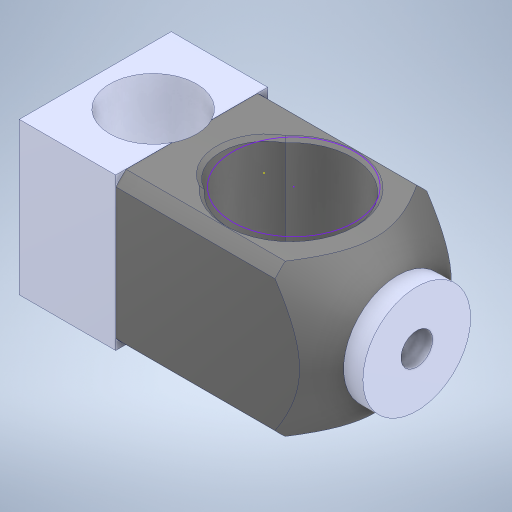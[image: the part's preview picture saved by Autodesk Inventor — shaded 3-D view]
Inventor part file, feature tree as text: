
AUTODESK INVENTOR PART (.ipt)
format: ipt  version: 2023 (Build 270158000, 158)  size: 342,528 bytes
history: mixed  units: in
note: dims shown in document units (in); Inventor stores cm internally (conversion verified against a paired STEP export)
features: sketch x8, extrude x7, other x1, imported_body x1
ambient origin geometry x8: Origin, YZ Plane, XZ Plane, XY Plane, X Axis, Y Axis, Z Axis, Center Point
bodies: Solid1 (imported_parasolid)
feature tree (17):
  other  "6669-001-1-solid1"
  extrude  "Extrusion1"  Depth=0.3937in
  sketch  "Sketch2"  dims[d8=0.3937in d9=0.0in d10=0.0in d11=0.0in]
  extrude  "Extrusion4"  TaperAngle=0.0deg  [1 undecoded]
  sketch  "Sketch5"  dims[d16=0.2362in d17=0.1969in]
  extrude  "Extrusion5"  Depth=0.3937in TaperAngle=0.0deg
  extrude  "Extrusion6"  Depth=0.1969in
  extrude  "Extrusion7"  Depth=0.3543in
  extrude  "Extrusion8"  Depth=0.0197in
  extrude  "Extrusion9"  Depth=0.0197in
  sketch  "Sketch1"  dims[d0=0.3937in d1=0.0in d7=0.1299in]
  sketch  "Sketch4"  dims[d12=0.0787in d13=0.0in d14=0.3937in d15=0.0in]
  sketch  "Sketch6"  dims[d18=0.1969in d19=0.0in d20=0.3543in]
  sketch  "Sketch7"  dims[d21=0.0in d22=0.0in d2=0.0197in]
  sketch  "Sketch8"  dims[d3=0.0344in d4=0.0197in]
  sketch  "Sketch9"  dims[d5=0.0344in]
  imported_body  NMx_Import_Brep_tag  [imported B-rep: ~14 faces, bbox_mm=[22.836, 10.765997, 12.379599]]
note: 1 required parameter value undecoded (feature->parameter linkage not recoverable at this tier; creation-order binding heuristic only, values carry confidence <= 0.55)
